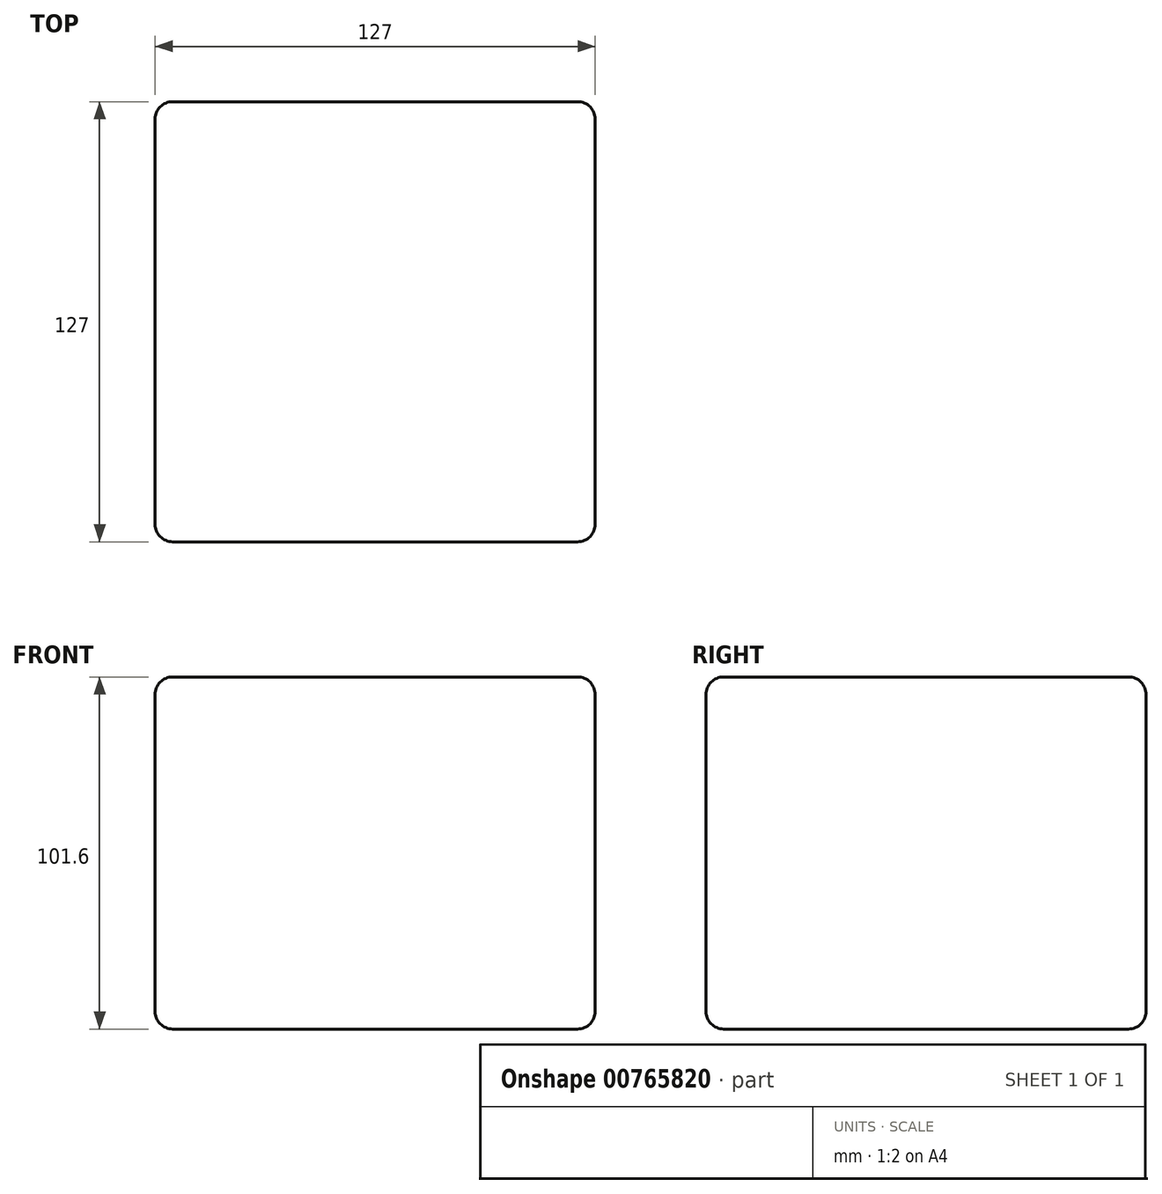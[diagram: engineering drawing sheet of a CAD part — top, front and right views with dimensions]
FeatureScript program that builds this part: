
annotation { "Feature Type Name" : "Feature", "Feature Type Description" : "" }
export const myFeature = defineFeature(function(context is Context, id is Id, definition is map)
    precondition{}
    {
        {
            var Q0;
            Q0=qCreatedBy(makeId("Top.planeOp"),FACE);
            var sketch = newSketch(context, id + "F0", { "sketchPlane" : qUnion([Q0])});
            skLineSegment(sketch, "E0.bottom", {"start": v(0, 0) * mm, "end": v(-127, 0) * mm});
            skLineSegment(sketch, "E0.top", {"start": v(0, 127) * mm, "end": v(-127, 127) * mm});
            skLineSegment(sketch, "E0.left", {"start": v(0, 0) * mm, "end": v(0, 127) * mm});
            skLineSegment(sketch, "E0.right", {"start": v(-127, 0) * mm, "end": v(-127, 127) * mm});
            skSolve(sketch);
        }
        {
            var Q0;
            Q0=makeQuery(id+"F0.imprint","IMPRINT",FACE,{"disambiguationData":[TD([[makeQuery(id+"F0.imprint","IMPRINT",EDGE,{"derivedFrom":sQuery(id+"F0.wireOp",EDGE,"E0.bottom")}),-1.0]])]});
            extrude(context, id + "F1", {"entities" : qUnion([Q0]), "depth" : 101.6 * mm, "offsetDistance" : 25.4 * mm});
        }
        {
            var Q0;
            Q0=makeQuery(id+"F1.opExtrude","CAP_EDGE",EDGE,{"disambiguationData":[OSD([sQuery(id+"F0.wireOp",EDGE,"E0.left")])],"isStart":false});
            var Q1;
            Q1=makeQuery(id+"F1.opExtrude","SWEPT_EDGE",EDGE,{"disambiguationData":[OSD([sQuery(id+"F0.wireOp",EDGE,"E0.bottom"),sQuery(id+"F0.wireOp",EDGE,"E0.left")])]});
            fillet(context, id + "F2", {"entities" : qUnion([Q0, Q1]), "radius" : 5.08 * mm, "tangentPropagation" : true, "allowEdgeOverflow" : false});
        }
        {
            var Q0;
            Q0=makeQuery(id+"F1.opExtrude","SWEPT_EDGE",EDGE,{"disambiguationData":[OSD([sQuery(id+"F0.wireOp",EDGE,"E0.bottom"),sQuery(id+"F0.wireOp",EDGE,"E0.right")])]});
            fillet(context, id + "F3", {"entities" : qUnion([Q0]), "radius" : 5.08 * mm, "tangentPropagation" : true, "allowEdgeOverflow" : false});
        }
        {
            var Q0;
            Q0=makeQuery(id+"F1.opExtrude","CAP_EDGE",EDGE,{"disambiguationData":[OSD([sQuery(id+"F0.wireOp",EDGE,"E0.right")])],"isStart":false});
            var Q1;
            Q1=makeQuery(id+"F1.opExtrude","SWEPT_EDGE",EDGE,{"disambiguationData":[OSD([sQuery(id+"F0.wireOp",EDGE,"E0.top"),sQuery(id+"F0.wireOp",EDGE,"E0.right")])]});
            fillet(context, id + "F4", {"entities" : qUnion([Q0, Q1]), "radius" : 5.08 * mm, "tangentPropagation" : true, "allowEdgeOverflow" : false});
        }
        {
            var Q0;
            Q0=makeQuery(id+"F1.opExtrude","CAP_EDGE",EDGE,{"disambiguationData":[OSD([sQuery(id+"F0.wireOp",EDGE,"E0.top")])],"isStart":false});
            var Q1;
            Q1=makeQuery(id+"F1.opExtrude","SWEPT_EDGE",EDGE,{"disambiguationData":[OSD([sQuery(id+"F0.wireOp",EDGE,"E0.top"),sQuery(id+"F0.wireOp",EDGE,"E0.left")])]});
            fillet(context, id + "F5", {"entities" : qUnion([Q0, Q1]), "radius" : 5.08 * mm, "tangentPropagation" : true, "allowEdgeOverflow" : false});
        }
        {
            var Q0;
            Q0=makeQuery(id+"F1.opExtrude","CAP_EDGE",EDGE,{"disambiguationData":[OSD([sQuery(id+"F0.wireOp",EDGE,"E0.left")])],"isStart":true});
            var Q1;
            Q1=makeQuery(id+"F1.opExtrude","CAP_FACE",FACE,{"disambiguationData":[OSD([sQuery(id+"F0.wireOp",EDGE,"E0.bottom"),sQuery(id+"F0.wireOp",EDGE,"E0.top"),sQuery(id+"F0.wireOp",EDGE,"E0.left"),sQuery(id+"F0.wireOp",EDGE,"E0.right")])],"isStart":true});
            fillet(context, id + "F6", {"entities" : qUnion([Q0, Q1]), "radius" : 5.08 * mm, "tangentPropagation" : true, "allowEdgeOverflow" : false});
        }
    });
